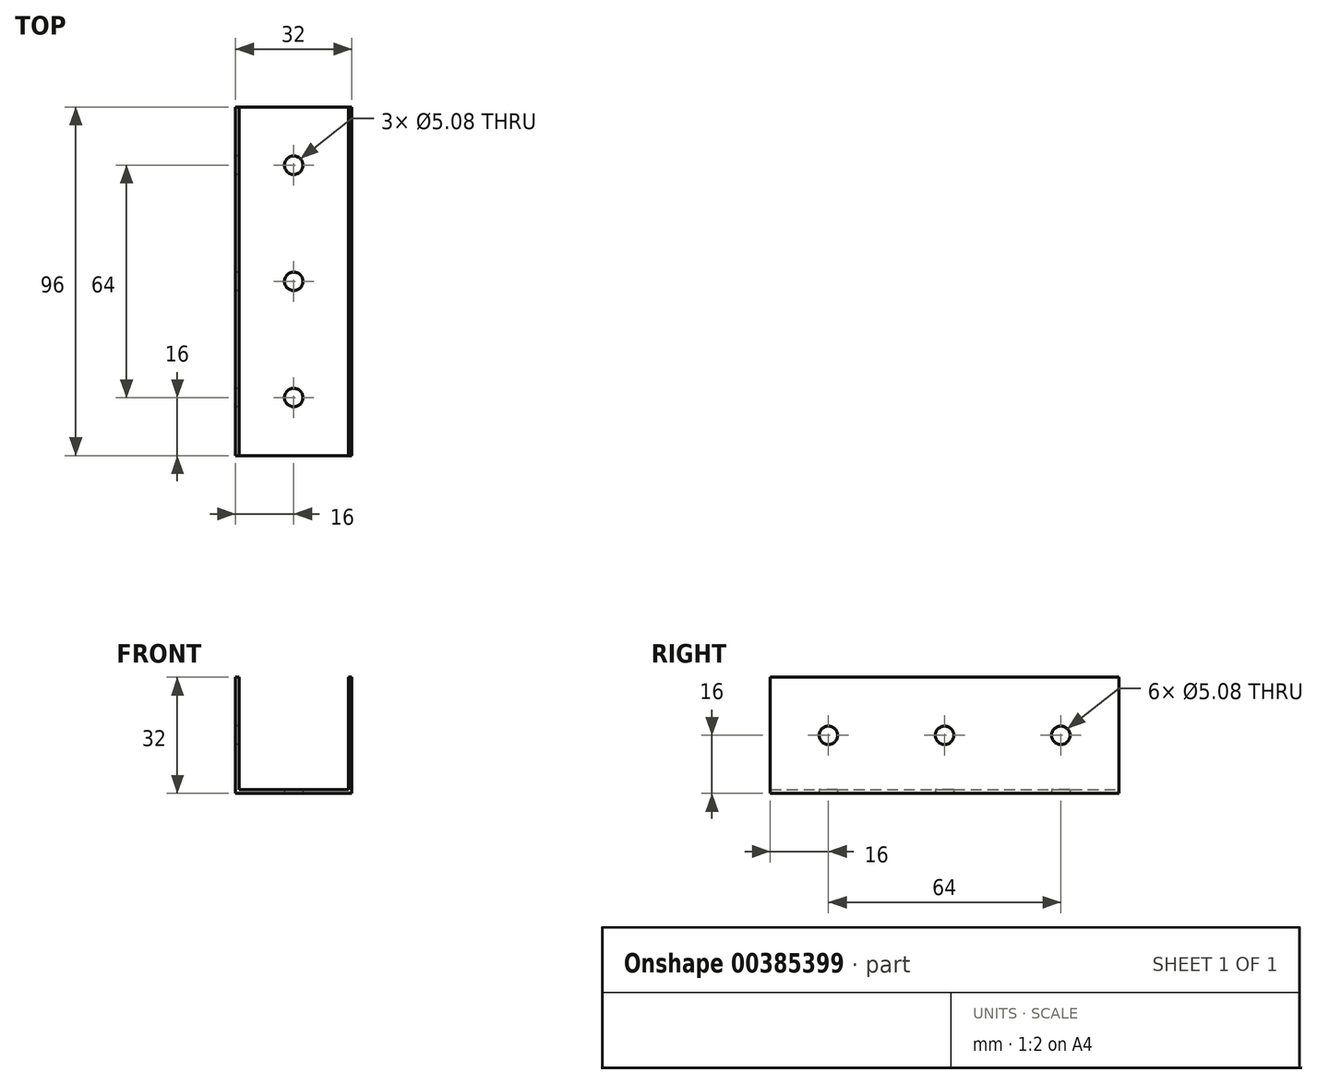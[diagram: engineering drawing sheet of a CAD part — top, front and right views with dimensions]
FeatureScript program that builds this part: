
annotation { "Feature Type Name" : "Feature", "Feature Type Description" : "" }
export const myFeature = defineFeature(function(context is Context, id is Id, definition is map)
    precondition{}
    {
        {
            var Q0;
            Q0=qCreatedBy(makeId("Front.planeOp"),FACE);
            var sketch = newSketch(context, id + "F0", { "sketchPlane" : qUnion([Q0])});
            skLineSegment(sketch, "E0", {"start": v(-16, 15.75) * mm, "end": v(-16, -16.25) * mm});
            skLineSegment(sketch, "E1", {"start": v(-16, -16.25) * mm, "end": v(16, -16.25) * mm});
            skLineSegment(sketch, "E2", {"start": v(16, -16.25) * mm, "end": v(16, 15.75) * mm});
            skLineSegment(sketch, "E3", {"start": v(16, 15.75) * mm, "end": v(15, 15.75) * mm});
            skLineSegment(sketch, "E4", {"start": v(15, 15.75) * mm, "end": v(15, -15.25) * mm});
            skLineSegment(sketch, "E5", {"start": v(15, -15.25) * mm, "end": v(-15, -15.25) * mm});
            skLineSegment(sketch, "E6", {"start": v(-15, -15.25) * mm, "end": v(-15, 15.75) * mm});
            skLineSegment(sketch, "E7", {"start": v(-15, 15.75) * mm, "end": v(-16, 15.75) * mm});
            skSolve(sketch);
        }
        {
            var Q0;
            Q0=qSketchRegion(id+"F0",true);
            extrude(context, id + "F1", {"entities" : qUnion([Q0]), "depth" : 96 * mm});
        }
        {
            var Q0;
            Q0=makeQuery(id+"F1.opExtrude","SWEPT_FACE",FACE,{"disambiguationData":[OSD([sQuery(id+"F0.wireOp",EDGE,"E0")])]});
            var sketch = newSketch(context, id + "F2", { "sketchPlane" : qUnion([Q0])});
            skPoint(sketch, "E8", {"position": v(16, -0.25) * mm});
            skCircle(sketch, "E9", {"center": v(16, -0.25) * mm, "radius": 2.54 * mm});
            skSolve(sketch);
        }
        {
            var Q0;
            Q0=makeQuery(id+"F2.imprint","IMPRINT",FACE,{"disambiguationData":[TD([[makeQuery(id+"F2.imprint","IMPRINT",EDGE,{"derivedFrom":sQuery(id+"F2.wireOp",EDGE,"E9")}),1.0]])]});
            extrude(context, id + "F3", {"entities" : qUnion([Q0]), "operationType" : NewBodyOperationType.REMOVE, "oppositeDirection" : true, "depth" : 50.8 * mm});
        }
        {
            var Q0;
            Q0=makeQuery(id+"F1.opExtrude","SWEPT_FACE",FACE,{"disambiguationData":[OSD([sQuery(id+"F0.wireOp",EDGE,"E0")])]});
            var sketch = newSketch(context, id + "F4", { "sketchPlane" : qUnion([Q0])});
            skPoint(sketch, "E10", {"position": v(32, 15.75) * mm});
            skPoint(sketch, "E11", {"position": v(64, 15.75) * mm});
            skPoint(sketch, "E12", {"position": v(32, -16.25) * mm});
            skPoint(sketch, "E13", {"position": v(64, -16.25) * mm});
            skPoint(sketch, "E14", {"position": v(48, -0.25) * mm});
            skPoint(sketch, "E15", {"position": v(80, -0.25) * mm});
            skCircle(sketch, "E16", {"center": v(48, -0.25) * mm, "radius": 2.54 * mm});
            skCircle(sketch, "E17", {"center": v(80, -0.25) * mm, "radius": 2.54 * mm});
            skSolve(sketch);
        }
        {
            var Q0;
            Q0=makeQuery(id+"F4.imprint","IMPRINT",FACE,{"disambiguationData":[TD([[makeQuery(id+"F4.imprint","IMPRINT",EDGE,{"derivedFrom":sQuery(id+"F4.wireOp",EDGE,"E16")}),1.0]])]});
            var Q1;
            Q1=qSketchRegion(id+"F4",true);
            extrude(context, id + "F5", {"entities" : qUnion([Q0, Q1]), "operationType" : NewBodyOperationType.REMOVE, "oppositeDirection" : true, "depth" : 50.8 * mm});
        }
        {
            var Q0;
            Q0=makeQuery(id+"F1.opExtrude","SWEPT_FACE",FACE,{"disambiguationData":[OSD([sQuery(id+"F0.wireOp",EDGE,"E1")])]});
            var sketch = newSketch(context, id + "F6", { "sketchPlane" : qUnion([Q0])});
            skPoint(sketch, "E18", {"position": v(16, 32) * mm});
            skPoint(sketch, "E19", {"position": v(16, 64) * mm});
            skPoint(sketch, "E20", {"position": v(-16, 64) * mm});
            skPoint(sketch, "E21", {"position": v(-16, 32) * mm});
            skPoint(sketch, "E22", {"position": v(0, 80) * mm});
            skPoint(sketch, "E23", {"position": v(0, 48) * mm});
            skPoint(sketch, "E24", {"position": v(0, 16) * mm});
            skCircle(sketch, "E25", {"center": v(0, 80) * mm, "radius": 2.54 * mm});
            skCircle(sketch, "E26", {"center": v(0, 48) * mm, "radius": 2.54 * mm});
            skCircle(sketch, "E27", {"center": v(0, 16) * mm, "radius": 2.54 * mm});
            skSolve(sketch);
        }
        {
            var Q0;
            Q0=makeQuery(id+"F6.imprint","IMPRINT",FACE,{"disambiguationData":[TD([[makeQuery(id+"F6.imprint","IMPRINT",EDGE,{"derivedFrom":sQuery(id+"F6.wireOp",EDGE,"E25")}),1.0]])]});
            var Q1;
            Q1=qSketchRegion(id+"F6",true);
            extrude(context, id + "F7", {"entities" : qUnion([Q0, Q1]), "operationType" : NewBodyOperationType.REMOVE, "oppositeDirection" : true, "depth" : 25.4 * mm});
        }
    });
